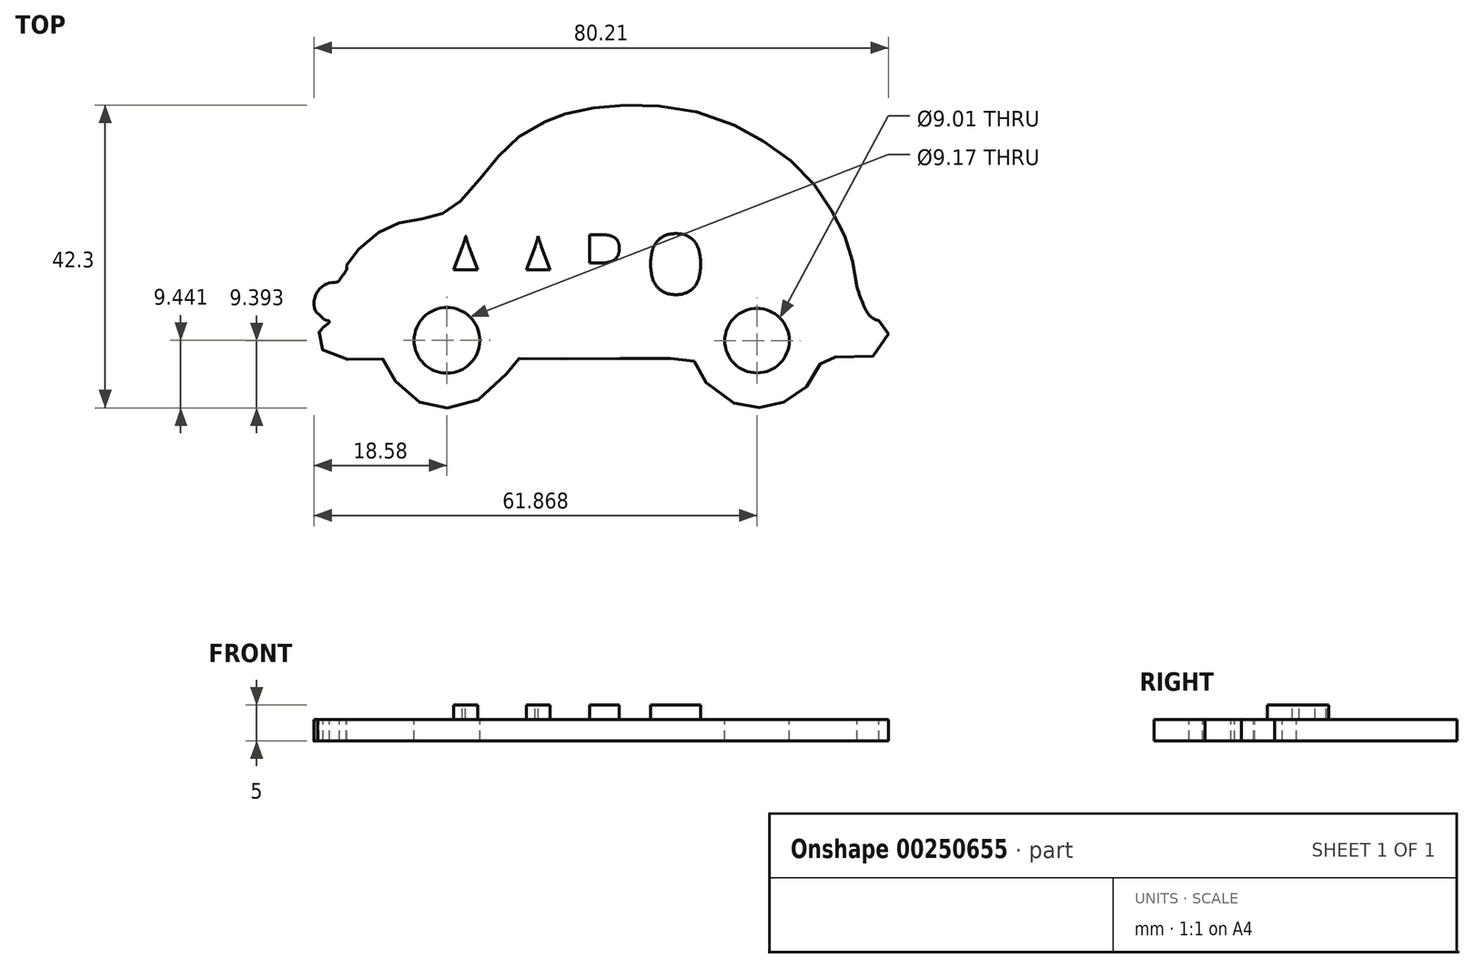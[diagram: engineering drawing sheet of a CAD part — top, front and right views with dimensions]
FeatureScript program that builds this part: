
annotation { "Feature Type Name" : "Feature", "Feature Type Description" : "" }
export const myFeature = defineFeature(function(context is Context, id is Id, definition is map)
    precondition{}
    {
        {
            var Q0;
            Q0=qCreatedBy(makeId("Top.planeOp"),FACE);
            var sketch = newSketch(context, id + "F0", { "sketchPlane" : qUnion([Q0])});
            skFitSpline(sketch, "E0", {"points": [v(-30.5, 4.35) * mm, v(-28.41, 6.9) * mm, v(-26.22, 8.39) * mm, v(-24.27, 9.39) * mm, v(-21.68, 9.84) * mm, v(-19.53, 10.34) * mm, v(-17.64, 10.83) * mm, v(-16.04, 11.73) * mm, v(-13.8, 13.98) * mm, v(-11.15, 17.27) * mm, v(-8.8, 19.92) * mm, v(-5.81, 22.41) * mm, v(-2.47, 24.06) * mm, v(-0.82, 24.7) * mm, v(2.37, 25.45) * mm, v(6.91, 25.94) * mm, v(11.75, 25.94) * mm, v(18.19, 24.96) * mm, v(24.38, 22.56) * mm, v(28.42, 20.12) * mm, v(32.46, 16.92) * mm, v(35.45, 13.23) * mm, v(37.56, 9.76) * mm, v(38.94, 6.61) * mm, v(39.74, 3.47) * mm, v(40.28, 0.53) * mm, v(40.5, 0.63) * mm, v(40.93, 0.82) * mm, v(42.24, 0.88) * mm, v(43.26, 0.42) * mm, v(43.93, -0.5) * mm, v(44.07, -2.97) * mm, v(43.5, -3.87) * mm, v(43.3, -4.1) * mm, v(43.65, -4.38) * mm, v(44.28, -4.92) * mm, v(44.59, -5.53) * mm, v(44.37, -7.5) * mm, v(42.92, -8.9) * mm, v(39.85, -9.16) * mm, v(36.35, -9.17) * mm, v(35.5, -9.18) * mm, v(35.31, -9.33) * mm, v(35.03, -10.5) * mm, v(34.3, -11.98) * mm, v(33.05, -13.49) * mm, v(31.5, -14.66) * mm, v(29.86, -15.55) * mm, v(28.26, -16.07) * mm, v(26.63, -16.26) * mm, v(25.4, -16.26) * mm, v(23.54, -15.8) * mm, v(20.8, -14.29) * mm, v(18.91, -12.38) * mm, v(18.2, -11.1) * mm, v(17.53, -9.8) * mm, v(17.36, -9.32) * mm, v(17.2, -9.33) * mm, v(14.18, -9.4) * mm, v(7.68, -9.4) * mm, v(0.4, -9.44) * mm, v(-6.06, -9.39) * mm, v(-7.6, -9.33) * mm, v(-7.87, -9.36) * mm, v(-8.61, -11.4) * mm, v(-11.21, -14.2) * mm, v(-14.28, -15.9) * mm, v(-16.7, -16.26) * mm, v(-17.97, -16.26) * mm, v(-20.28, -15.69) * mm, v(-22.5, -14.32) * mm, v(-24.33, -12.42) * mm, v(-25.5, -10.36) * mm, v(-25.9, -9.5) * mm, v(-26.2, -9.5) * mm, v(-29.93, -9.5) * mm, v(-32.86, -9.29) * mm, v(-34.14, -8.43) * mm, v(-34.86, -7.42) * mm, v(-35.05, -6.58) * mm, v(-34.88, -5.56) * mm, v(-34.31, -5.03) * mm, v(-33.4, -4.23) * mm, v(-33.95, -4.04) * mm, v(-34.65, -3.44) * mm, v(-35.41, -2.62) * mm, v(-35.41, -0.72) * mm, v(-34.37, 0.7) * mm, v(-33.18, 1.2) * mm, v(-32.23, 1.33) * mm, v(-32.03, 1.6) * mm, v(-31.05, 3.57) * mm, v(-30.5, 4.35) * mm]});
            skCircle(sketch, "E1", {"center": v(-17, -6.85) * mm, "radius": 4.59 * mm});
            skPoint(sketch, "E1.first.point", {"position": v(-21.58, -7) * mm});
            skPoint(sketch, "E1.second.point", {"position": v(-18.62, -2.56) * mm});
            skPoint(sketch, "E1.third.point", {"position": v(-13.1, -9.26) * mm});
            skCircle(sketch, "E2", {"center": v(26.29, -6.9) * mm, "radius": 4.5 * mm});
            skPoint(sketch, "E2.first.point", {"position": v(22.2, -4.99) * mm});
            skPoint(sketch, "E2.second.point", {"position": v(30.4, -5.05) * mm});
            skPoint(sketch, "E2.third.point", {"position": v(26.12, -11.4) * mm});
            skFitSpline(sketch, "E3", {"points": [v(43.3, -4.1) * mm, v(42.81, -3.94) * mm, v(42.34, -3.67) * mm, v(41.63, -2.92) * mm, v(41, -1.55) * mm, v(40.28, 0.53) * mm, v(40.13, 2.95) * mm, v(40.72, 3.39) * mm, v(46.6, -2.51) * mm, v(45.1, -5.11) * mm, v(44.8, -4.55) * mm, v(43.3, -4.1) * mm]});
            skFitSpline(sketch, "E4", {"points": [v(-11.54, 10.5) * mm, v(-8.03, 10.52) * mm, v(-2.54, 10.52) * mm, v(5.06, 10.52) * mm, v(5.31, 10.5) * mm, v(5.45, 10.52) * mm, v(5.58, 12.27) * mm, v(5.58, 17.38) * mm, v(5.45, 22.31) * mm, v(5.45, 22.65) * mm, v(5.4, 22.8) * mm, v(4.94, 22.84) * mm, v(3.3, 22.8) * mm, v(1.23, 22.57) * mm, v(-1.14, 21.72) * mm, v(-2.95, 20.63) * mm, v(-4.65, 19.32) * mm, v(-6.13, 18.1) * mm, v(-7.77, 16.22) * mm, v(-8.84, 14.88) * mm, v(-9.94, 13.35) * mm, v(-10.89, 11.9) * mm, v(-11.45, 10.82) * mm, v(-11.52, 10.66) * mm, v(-11.54, 10.5) * mm]});
            skFitSpline(sketch, "E5", {"points": [v(9.1, 23.03) * mm, v(10.03, 23.1) * mm, v(12.1, 23.03) * mm, v(14.5, 22.7) * mm, v(16.87, 22.11) * mm, v(19.52, 21.23) * mm, v(23.01, 19.68) * mm, v(26, 17.84) * mm, v(28.44, 15.8) * mm, v(30.42, 13.75) * mm, v(31.87, 12.2) * mm, v(33.17, 10.47) * mm, v(32.57, 10.4) * mm, v(23.64, 10.42) * mm, v(15.23, 10.42) * mm, v(11.16, 10.47) * mm, v(9.65, 10.42) * mm, v(9.32, 10.47) * mm, v(9.22, 11.85) * mm, v(9.14, 22.3) * mm, v(9.14, 22.69) * mm, v(9.1, 22.9) * mm, v(9.1, 23.03) * mm]});
            skText(sketch, "E6", { "text": "ARON", "fontName": "OpenSans-Regular.ttf"});
            skText(sketch, "E7", { "text": "A", "fontName": "OpenSans-Regular.ttf"});
            skFitSpline(sketch, "E8", {"points": [v(-34.31, -5.03) * mm, v(-33.43, -4.3) * mm, v(-33.4, -4.23) * mm, v(-33.32, -4.22) * mm, v(-32.96, -4.11) * mm, v(-32.85, -3.55) * mm, v(-32.9, -1.3) * mm, v(-32.5, 0.29) * mm, v(-32.03, 1.6) * mm, v(-31.05, 3.57) * mm, v(-37.35, 1.83) * mm, v(-34.88, -5.56) * mm, v(-34.31, -5.03) * mm]});
            const initialGuessF0  = {"E6": [-0.00886, -0.00138, 1, 0, 0.01044], "E7": [-0.01897, -0.00138, 1, 0, 0.01044]};
            skSetInitialGuess(sketch, initialGuessF0);
            skSolve(sketch);
        }
        {
            var Q0;
            Q0=makeQuery(id+"F0.imprint","IMPRINT",FACE,{"disambiguationData":[TD([[makeQuery(id+"F0.imprint","IMPRINT",EDGE,{"derivedFrom":sQuery(id+"F0.wireOp",EDGE,"E1")}),-1.0]])]});
            var Q1;
            Q1=makeQuery(id+"F0.imprint","IMPRINT",FACE,{"disambiguationData":[TD([[makeQuery(id+"F0.imprint","IMPRINT",EDGE,{"derivedFrom":sQuery(id+"F0.wireOp",EDGE,"E4")}),1.0]])]});
            var Q2;
            Q2=makeQuery(id+"F0.imprint","IMPRINT",FACE,{"disambiguationData":[TD([[makeQuery(id+"F0.imprint","IMPRINT",EDGE,{"derivedFrom":sQuery(id+"F0.wireOp",EDGE,"E5")}),-1.0]])]});
            var Q3;
            {var subQ0=sQuery(id+"F0.wireOp",EDGE,"152ad286-1f57-4020-8d08-6a7d6f7e2b62");var subQ1=sQuery(id+"F0.wireOp",EDGE,"E0");var subQ2=makeQuery(id+"F0.imprint","INTERSECT",VERTEX,{"disambiguationData":[OD(0.0)],"derivedFrom":[subQ1,subQ0]});Q3=makeQuery(id+"F0.imprint","IMPRINT",FACE,{"disambiguationData":[TD([[makeQuery(id+"F0.imprint","IMPRINT",EDGE,{"disambiguationData":[TD([[subQ2,-1.0]])],"derivedFrom":subQ1}),-1.0]])]});}
            var Q4;
            {var subQ0=sQuery(id+"F0.wireOp",EDGE,"E3");var subQ1=sQuery(id+"F0.wireOp",EDGE,"E0");var subQ2=makeQuery(id+"F0.imprint","INTERSECT",VERTEX,{"disambiguationData":[OD(0.0)],"derivedFrom":[subQ1,subQ0]});Q4=makeQuery(id+"F0.imprint","IMPRINT",FACE,{"disambiguationData":[TD([[makeQuery(id+"F0.imprint","IMPRINT",EDGE,{"disambiguationData":[TD([[subQ2,1.0]])],"derivedFrom":subQ1}),-1.0]])]});}
            var Q5;
            Q5=makeQuery(id+"F0.imprint","IMPRINT",FACE,{"disambiguationData":[TD([[makeQuery(id+"F0.imprint","IMPRINT",EDGE,{"derivedFrom":sQuery(id+"F0.wireOp",EDGE,"E6.sketch_text.stroke-39")}),1.0]])]});
            var Q6;
            Q6=makeQuery(id+"F0.imprint","IMPRINT",FACE,{"disambiguationData":[TD([[makeQuery(id+"F0.imprint","IMPRINT",EDGE,{"derivedFrom":sQuery(id+"F0.wireOp",EDGE,"E6.sketch_text.stroke-31")}),-1.0]])]});
            var Q7;
            Q7=makeQuery(id+"F0.imprint","IMPRINT",FACE,{"disambiguationData":[TD([[makeQuery(id+"F0.imprint","IMPRINT",EDGE,{"derivedFrom":sQuery(id+"F0.wireOp",EDGE,"E6.sketch_text.stroke-47")}),-1.0]])]});
            var Q8;
            Q8=makeQuery(id+"F0.imprint","IMPRINT",FACE,{"disambiguationData":[TD([[makeQuery(id+"F0.imprint","IMPRINT",EDGE,{"derivedFrom":sQuery(id+"F0.wireOp",EDGE,"E6.sketch_text.stroke-24")}),1.0]])]});
            var Q9;
            Q9=makeQuery(id+"F0.imprint","IMPRINT",FACE,{"disambiguationData":[TD([[makeQuery(id+"F0.imprint","IMPRINT",EDGE,{"derivedFrom":sQuery(id+"F0.wireOp",EDGE,"E6.sketch_text.stroke-13")}),-1.0]])]});
            var Q10;
            Q10=makeQuery(id+"F0.imprint","IMPRINT",FACE,{"disambiguationData":[TD([[makeQuery(id+"F0.imprint","IMPRINT",EDGE,{"derivedFrom":sQuery(id+"F0.wireOp",EDGE,"E6.sketch_text.stroke-8")}),1.0]])]});
            var Q11;
            Q11=makeQuery(id+"F0.imprint","IMPRINT",FACE,{"disambiguationData":[TD([[makeQuery(id+"F0.imprint","IMPRINT",EDGE,{"derivedFrom":sQuery(id+"F0.wireOp",EDGE,"E6.sketch_text.stroke-0")}),-1.0]])]});
            var Q12;
            Q12=makeQuery(id+"F0.imprint","IMPRINT",FACE,{"disambiguationData":[TD([[makeQuery(id+"F0.imprint","IMPRINT",EDGE,{"derivedFrom":sQuery(id+"F0.wireOp",EDGE,"E7.sketch_text.stroke-8")}),1.0]])]});
            var Q13;
            Q13=makeQuery(id+"F0.imprint","IMPRINT",FACE,{"disambiguationData":[TD([[makeQuery(id+"F0.imprint","IMPRINT",EDGE,{"derivedFrom":sQuery(id+"F0.wireOp",EDGE,"E7.sketch_text.stroke-0")}),-1.0]])]});
            var Q14;
            {var subQ0=sQuery(id+"F0.wireOp",EDGE,"E8");var subQ1=sQuery(id+"F0.wireOp",EDGE,"E0");var subQ2=makeQuery(id+"F0.imprint","INTERSECT",VERTEX,{"disambiguationData":[OD(3.0)],"derivedFrom":[subQ1,subQ0]});Q14=makeQuery(id+"F0.imprint","IMPRINT",FACE,{"disambiguationData":[TD([[makeQuery(id+"F0.imprint","IMPRINT",EDGE,{"disambiguationData":[TD([[subQ2,-1.0]])],"derivedFrom":subQ1}),-1.0]])]});}
            var Q15;
            {var subQ0=sQuery(id+"F0.wireOp",EDGE,"E8");var subQ1=sQuery(id+"F0.wireOp",EDGE,"E0");var subQ2=makeQuery(id+"F0.imprint","INTERSECT",VERTEX,{"disambiguationData":[OD(1.0)],"derivedFrom":[subQ1,subQ0]});Q15=makeQuery(id+"F0.imprint","IMPRINT",FACE,{"disambiguationData":[TD([[makeQuery(id+"F0.imprint","IMPRINT",EDGE,{"disambiguationData":[TD([[subQ2,1.0]])],"derivedFrom":subQ1}),-1.0]])]});}
            var Q16;
            {var subQ0=sQuery(id+"F0.wireOp",EDGE,"E8");var subQ1=sQuery(id+"F0.wireOp",EDGE,"E0");var subQ2=makeQuery(id+"F0.imprint","INTERSECT",VERTEX,{"disambiguationData":[OD(0.0)],"derivedFrom":[subQ1,subQ0]});Q16=makeQuery(id+"F0.imprint","IMPRINT",FACE,{"disambiguationData":[TD([[makeQuery(id+"F0.imprint","IMPRINT",EDGE,{"disambiguationData":[TD([[subQ2,-1.0]])],"derivedFrom":subQ1}),-1.0]])]});}
            extrude(context, id + "F1", {"entities" : qUnion([Q0, Q1, Q2, Q3, Q4, Q5, Q6, Q7, Q8, Q9, Q10, Q11, Q12, Q13, Q14, Q15, Q16]), "oppositeDirection" : true, "depth" : 5 * mm});
        }
        {
            var Q0;
            {var subQ0=sQuery(id+"F0.wireOp",EDGE,"E3");var subQ1=sQuery(id+"F0.wireOp",EDGE,"E0");var subQ2=makeQuery(id+"F0.imprint","INTERSECT",VERTEX,{"disambiguationData":[OD(0.0)],"derivedFrom":[subQ1,subQ0]});Q0=makeQuery(id+"F0.imprint","IMPRINT",FACE,{"disambiguationData":[TD([[makeQuery(id+"F0.imprint","IMPRINT",EDGE,{"disambiguationData":[TD([[subQ2,1.0]])],"derivedFrom":subQ1}),-1.0]])]});}
            var Q1;
            {var subQ0=sQuery(id+"F0.wireOp",EDGE,"152ad286-1f57-4020-8d08-6a7d6f7e2b62");var subQ1=sQuery(id+"F0.wireOp",EDGE,"E0");var subQ2=makeQuery(id+"F0.imprint","INTERSECT",VERTEX,{"disambiguationData":[OD(0.0)],"derivedFrom":[subQ1,subQ0]});Q1=makeQuery(id+"F0.imprint","IMPRINT",FACE,{"disambiguationData":[TD([[makeQuery(id+"F0.imprint","IMPRINT",EDGE,{"disambiguationData":[TD([[subQ2,-1.0]])],"derivedFrom":subQ1}),-1.0]])]});}
            var Q2;
            Q2=makeQuery(id+"F0.imprint","IMPRINT",FACE,{"disambiguationData":[TD([[makeQuery(id+"F0.imprint","IMPRINT",EDGE,{"derivedFrom":sQuery(id+"F0.wireOp",EDGE,"E4")}),1.0]])]});
            var Q3;
            Q3=makeQuery(id+"F0.imprint","IMPRINT",FACE,{"disambiguationData":[TD([[makeQuery(id+"F0.imprint","IMPRINT",EDGE,{"derivedFrom":sQuery(id+"F0.wireOp",EDGE,"E5")}),-1.0]])]});
            var Q4;
            Q4=makeQuery(id+"F0.imprint","IMPRINT",FACE,{"disambiguationData":[TD([[makeQuery(id+"F0.imprint","IMPRINT",EDGE,{"derivedFrom":sQuery(id+"F0.wireOp",EDGE,"E7.sketch_text.stroke-0")}),-1.0]])]});
            var Q5;
            Q5=makeQuery(id+"F0.imprint","IMPRINT",FACE,{"disambiguationData":[TD([[makeQuery(id+"F0.imprint","IMPRINT",EDGE,{"derivedFrom":sQuery(id+"F0.wireOp",EDGE,"E6.sketch_text.stroke-0")}),-1.0]])]});
            var Q6;
            Q6=makeQuery(id+"F0.imprint","IMPRINT",FACE,{"disambiguationData":[TD([[makeQuery(id+"F0.imprint","IMPRINT",EDGE,{"derivedFrom":sQuery(id+"F0.wireOp",EDGE,"E6.sketch_text.stroke-13")}),-1.0]])]});
            var Q7;
            Q7=makeQuery(id+"F0.imprint","IMPRINT",FACE,{"disambiguationData":[TD([[makeQuery(id+"F0.imprint","IMPRINT",EDGE,{"derivedFrom":sQuery(id+"F0.wireOp",EDGE,"E6.sketch_text.stroke-31")}),-1.0]])]});
            var Q8;
            Q8=makeQuery(id+"F0.imprint","IMPRINT",FACE,{"disambiguationData":[TD([[makeQuery(id+"F0.imprint","IMPRINT",EDGE,{"derivedFrom":sQuery(id+"F0.wireOp",EDGE,"E6.sketch_text.stroke-47")}),-1.0]])]});
            var Q9;
            {var subQ0=sQuery(id+"F0.wireOp",EDGE,"E8");var subQ1=sQuery(id+"F0.wireOp",EDGE,"E0");var subQ2=makeQuery(id+"F0.imprint","INTERSECT",VERTEX,{"disambiguationData":[OD(3.0)],"derivedFrom":[subQ1,subQ0]});Q9=makeQuery(id+"F0.imprint","IMPRINT",FACE,{"disambiguationData":[TD([[makeQuery(id+"F0.imprint","IMPRINT",EDGE,{"disambiguationData":[TD([[subQ2,-1.0]])],"derivedFrom":subQ1}),-1.0]])]});}
            extrude(context, id + "F2", {"entities" : qUnion([Q0, Q1, Q2, Q3, Q4, Q5, Q6, Q7, Q8, Q9]), "operationType" : NewBodyOperationType.REMOVE, "oppositeDirection" : true, "depth" : 2 * mm});
        }
    });
